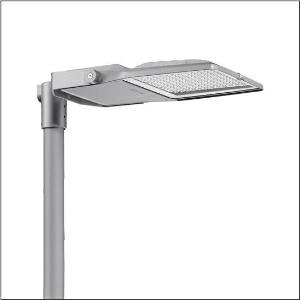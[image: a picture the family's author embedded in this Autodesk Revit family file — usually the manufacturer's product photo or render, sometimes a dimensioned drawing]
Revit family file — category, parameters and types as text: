
# Revit family: floodlight_fl_21_iq_midi___pl52_5xa7781e2d3a_77a1
name_source: partatom
category: Lighting Fixtures
units: mm (PartAtom-declared; Revit-internal decimal feet)

## family parameters
Cut with Voids When Loaded = No
Host = Face
Light Source = No
Part Type = Normal
Room Calculation Point = No
Round Connector Dimension = Use Diameter
Shared = No

## types (1)
- --- (1 x LED, 26850 lm, 208.1 W, 3000K)
    Apparent Load = 208 VA
    CIE Flux Codes = 26 60 98 100 100
    Color Rendering = 70
    Color Temperature = 3000K
    Default Elevation = 1800 mm
    Description = Floodlight FL 21 iQ midi, floodlight, primary light control with lens, of PMMA, primary optical cover: protective disc, of toughened safety glass, transparent, light distribution: PL52, light emission: direct distribution, installation type: surface-mounted, LED, High Power LED, rated luminous flux: 26.850lm, luminous efficacy: 129lm/W, light colour: 730, colour temperature: 3000K, control gear: ECG iQ, control: optimised constant luminous flux control (CLO 2.0), Desk-Remote (wireless, voltage-free reading and setting of iQ features in the workshop via application-optimized NFC function/RFID function), Light-Fading, Smart-Wire, Night-Set, Lumen-Switch, Temp-Guard, Auto-Match, with terminal, 6-pole, mains connection: 220..240V, AC, 50/60Hz, start of lifetime: 208W, end of service life: 227W, reduction: 90W, luminaire housing, of diecast aluminium, powder-coated, Siteco® metallic grey (DB 702S), corrosivity category C5 mid according to DIN EN ISO 12944, sealing non-destructively replaceable, please order mast flange separately, mast bracket, of steel, galvanised, powder-coated, Siteco® metallic grey (DB 702S), protection rating (complete): IP66, insulation class (complete): insulation class II (safety insulation), certification: CE, protection symbol: D, impact resistance: IK08, permissible operating ambient temperature: -40..+40°C, permissible operating ambient temperature for outdoor applications: -40..+50°C, standard: DIN EN 12944, LABS conformity tested according to VDMA 24364:2018-05, packaging unit: 1 piece

Light Distribution: PL52
    Height = 76 mm
    Lamp = 1 x LED
    Lamp Light Flux = 26850 lm
    Lamp Power = 208.1 W
    Lamp count = 1
    Length = 657 mm
    Luminous efficacy = 129 lm/W
    Manufacturer = Siteco
    ModVariant = No
    Model = 5XA7781E2D3A
    Number of Poles = 1
    OnlyDefault = Yes
    Power Factor = 1
    Product Name = Floodlight FL 21 iQ midi | PL52
    Product group = floodlight | pylon annexe
    ProductGroupID = 6200
    Protection Class = Protection class II
    Protection Degree = IP 66
    RLX_Detail_Level = 1
    RLX_Emergency_Light_Flux = 0 lm
    RLX_Emergency_Type = 0
    RLX_Emergency_Type_DB = No
    RlxData = <blob elided: 154189 chars, md5=235aa524>
    Socket = socket
    Standby Power = 0 W
    System Light Flux = 26850 lm
    System Power = 208 W
    Type Comments = factory setting: luminous flux: 100 % | dim-lin: 254 | 710 mA
    Type Image = l_1007123.jpg
    URL = http://relux.com
    VarID = @adj_054561
    Voltage = 0 V
    Weight = 0.00 kg
    Width = 442 mm

## geometry (parser evidence)
native form markers: Blend x4, Sweep x14
no freeform markers — native parametric forms only
